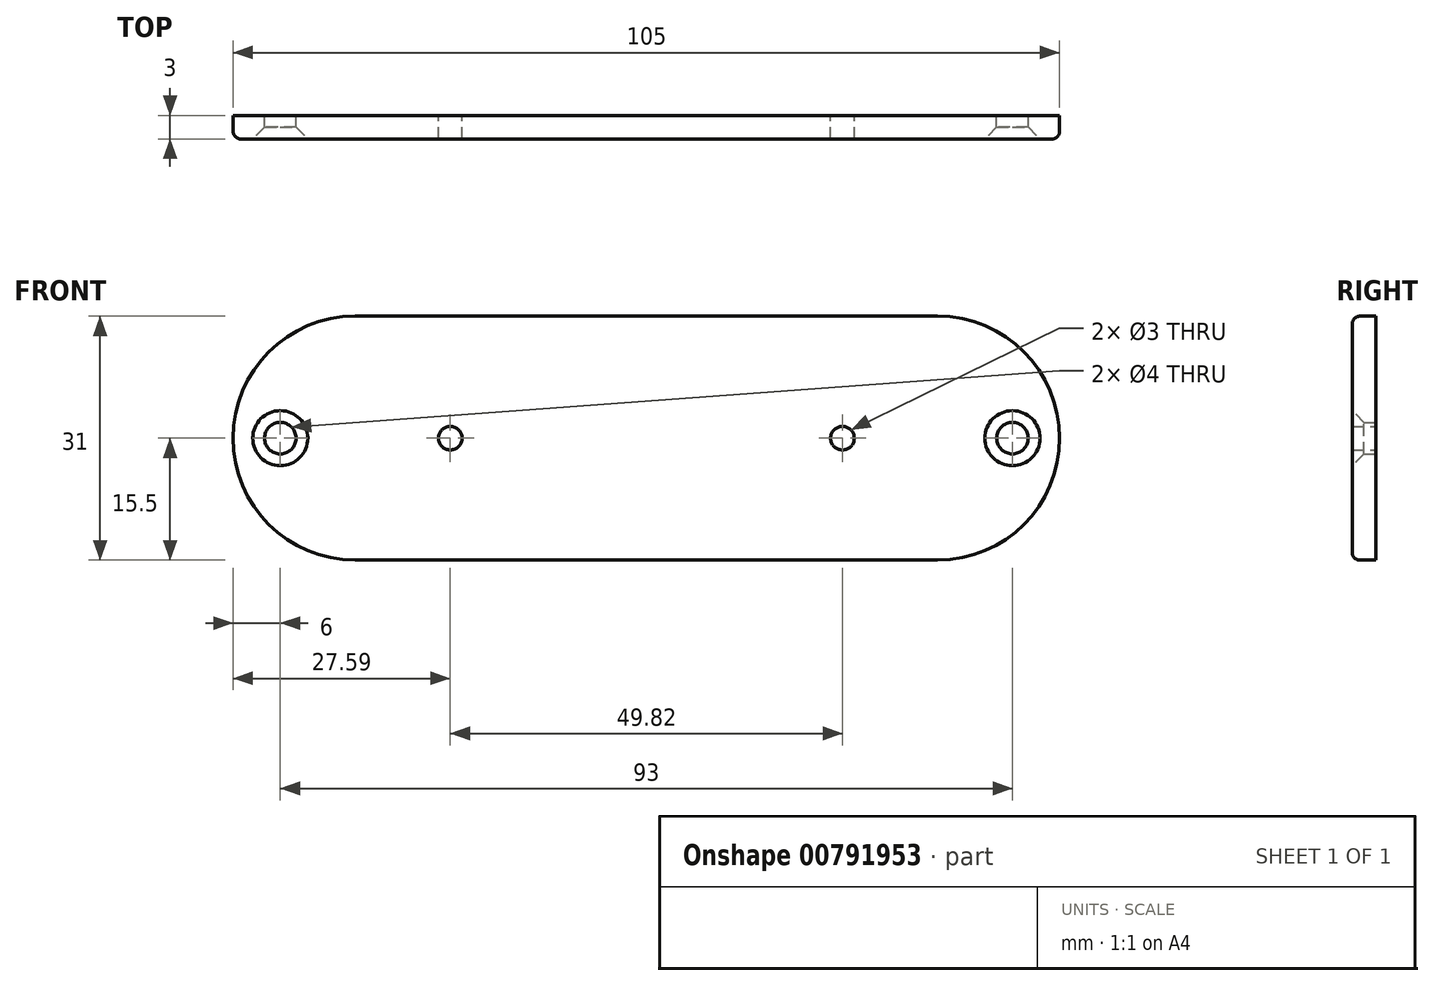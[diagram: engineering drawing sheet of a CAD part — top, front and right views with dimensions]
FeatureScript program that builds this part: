
annotation { "Feature Type Name" : "Feature", "Feature Type Description" : "" }
export const myFeature = defineFeature(function(context is Context, id is Id, definition is map)
    precondition{}
    {
        {
            var Q0;
            Q0=qCreatedBy(makeId("Front.planeOp"),FACE);
            var sketch = newSketch(context, id + "F0", { "sketchPlane" : qUnion([Q0])});
            skLineSegment(sketch, "E0.bottom", {"start": v(37, 15.5) * mm, "end": v(-37, 15.5) * mm});
            skLineSegment(sketch, "E0.top", {"start": v(37, -15.5) * mm, "end": v(-37, -15.5) * mm});
            skPoint(sketch, "E0.middle", {"position": v(0, 0) * mm});
            skArc(sketch, "E1", {"start": v(-37, 15.5) * mm, "mid": v(-52.5, 0) * mm, "end": v(-37, -15.5) * mm});
            skPoint(sketch, "E2.orphan", {"position": v(-52.5, 15.5) * mm});
            skPoint(sketch, "E3.orphan", {"position": v(-52.5, -15.5) * mm});
            skArc(sketch, "E4.MirrorCS", {"start": v(37, 15.5) * mm, "mid": v(52.5, 0) * mm, "end": v(37, -15.5) * mm});
            skPoint(sketch, "E5.orphan", {"position": v(52.5, 15.5) * mm});
            skPoint(sketch, "E6.orphan", {"position": v(52.5, -15.5) * mm});
            skCircle(sketch, "E7", {"center": v(24.91, 0) * mm, "radius": 1.5 * mm});
            skCircle(sketch, "E8", {"center": v(46.5, 0) * mm, "radius": 2 * mm});
            skCircle(sketch, "E9.MirrorC", {"center": v(-24.91, 0) * mm, "radius": 1.5 * mm});
            skCircle(sketch, "E10.MirrorC", {"center": v(-46.5, 0) * mm, "radius": 2 * mm});
            skSolve(sketch);
        }
        {
            var Q0;
            Q0 = qSketchRegion(id + "F0", true);
            extrude(context, id + "F1", {"entities" : qUnion([Q0]), "depth" : 3 * mm, "offsetDistance" : 25 * mm});
        }
        {
            var Q0;
            Q0=makeQuery(id+"F1.opExtrude","CAP_EDGE",EDGE,{"disambiguationData":[OSD([sQuery(id+"F0.wireOp",EDGE,"E1")])],"isStart":false});
            fillet(context, id + "F2", {"entities" : qUnion([Q0]), "radius" : 1 * mm, "tangentPropagation" : true, "allowEdgeOverflow" : false});
        }
        {
            var Q0;
            Q0=makeQuery(id+"F1.opExtrude","CAP_EDGE",EDGE,{"disambiguationData":[OSD([sQuery(id+"F0.wireOp",EDGE,"E10.MirrorC")])],"isStart":false});
            var Q1;
            Q1=makeQuery(id+"F1.opExtrude","CAP_EDGE",EDGE,{"disambiguationData":[OSD([sQuery(id+"F0.wireOp",EDGE,"E8")])],"isStart":false});
            chamfer(context, id + "F3", {"entities" : qUnion([Q0, Q1]), "width" : 1.5 * mm, "tangentPropagation" : true});
        }
    });
